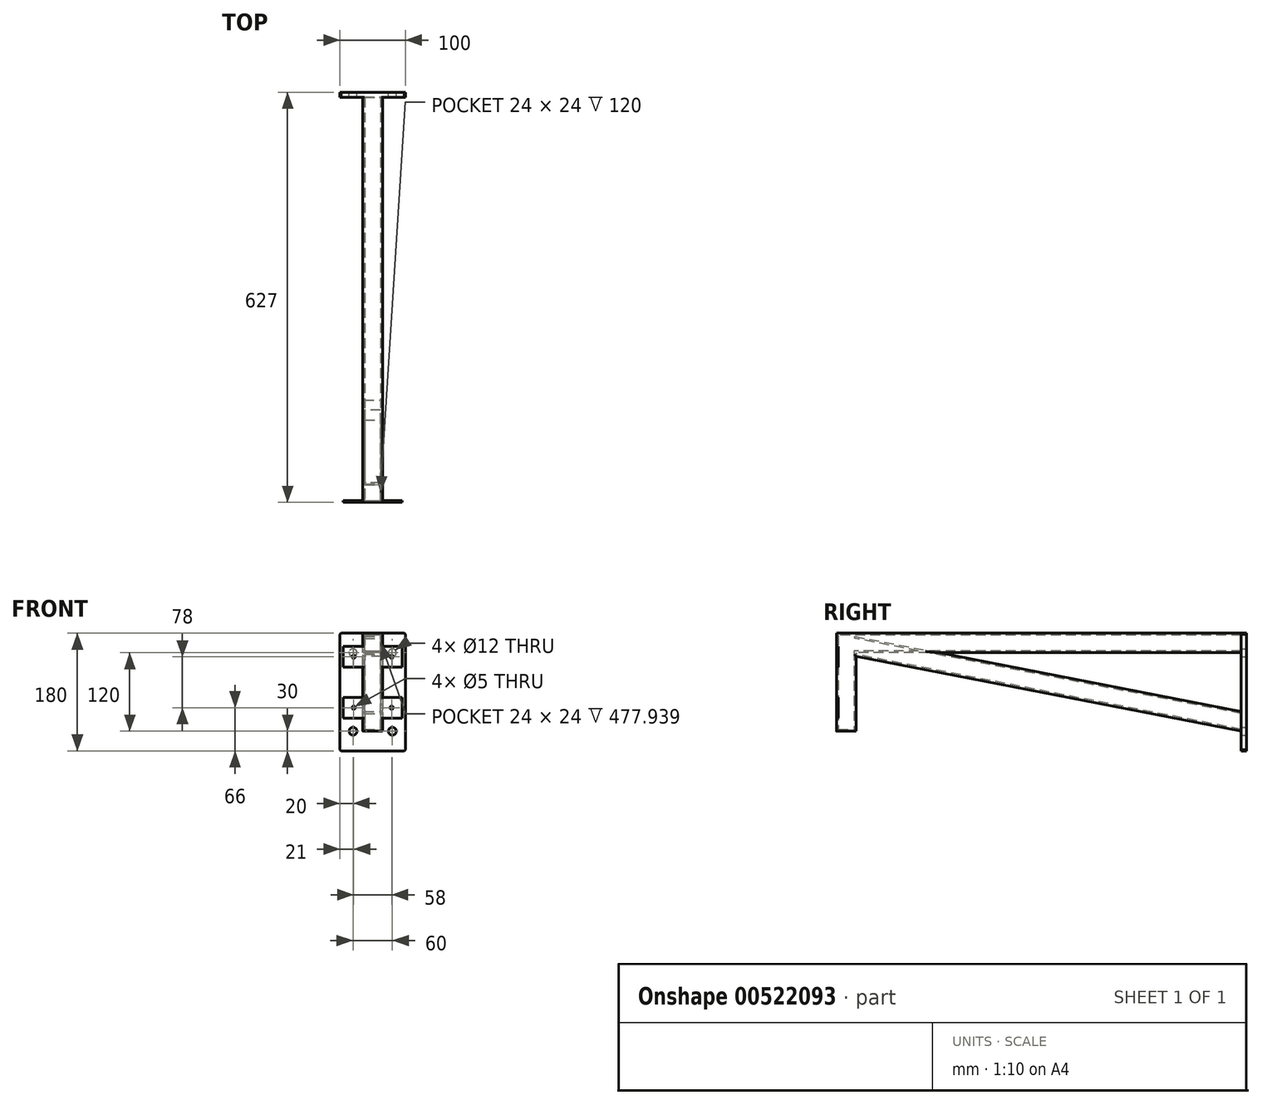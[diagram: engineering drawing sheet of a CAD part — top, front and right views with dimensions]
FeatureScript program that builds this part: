
annotation { "Feature Type Name" : "Feature", "Feature Type Description" : "" }
export const myFeature = defineFeature(function(context is Context, id is Id, definition is map)
    precondition{}
    {
        {
            var Q0;
            Q0=qCreatedBy(makeId("Front.planeOp"),FACE);
            var sketch = newSketch(context, id + "F0", { "sketchPlane" : qUnion([Q0])});
            skLineSegment(sketch, "E0.bottom", {"start": v(50, 90) * mm, "end": v(-50, 90) * mm});
            skLineSegment(sketch, "E0.top", {"start": v(50, -90) * mm, "end": v(-50, -90) * mm});
            skLineSegment(sketch, "E0.left", {"start": v(50, 90) * mm, "end": v(50, -90) * mm});
            skLineSegment(sketch, "E0.right", {"start": v(-50, 90) * mm, "end": v(-50, -90) * mm});
            skPoint(sketch, "E0.middle", {"position": v(0, 0) * mm});
            skCircle(sketch, "E1", {"center": v(-30, 60) * mm, "radius": 6 * mm});
            skCircle(sketch, "E2", {"center": v(30, 60) * mm, "radius": 6 * mm});
            skCircle(sketch, "E3", {"center": v(30, -60) * mm, "radius": 6 * mm});
            skCircle(sketch, "E4", {"center": v(-30, -60) * mm, "radius": 6 * mm});
            skSolve(sketch);
        }
        {
            var Q0;
            Q0 = qSketchRegion(id + "F0", true);
            extrude(context, id + "F1", {"entities" : qUnion([Q0]), "depth" : 8 * mm, "offsetDistance" : 25 * mm});
        }
        {
            var Q0;
            Q0=makeQuery(id+"F1.opExtrude","SWEPT_EDGE",EDGE,{"disambiguationData":[OSD([sQuery(id+"F0.wireOp",EDGE,"E0.bottom"),sQuery(id+"F0.wireOp",EDGE,"E0.left")])]});
            var Q1;
            Q1=makeQuery(id+"F1.opExtrude","SWEPT_EDGE",EDGE,{"disambiguationData":[OSD([sQuery(id+"F0.wireOp",EDGE,"E0.top"),sQuery(id+"F0.wireOp",EDGE,"E0.left")])]});
            var Q2;
            Q2=makeQuery(id+"F1.opExtrude","SWEPT_EDGE",EDGE,{"disambiguationData":[OSD([sQuery(id+"F0.wireOp",EDGE,"E0.top"),sQuery(id+"F0.wireOp",EDGE,"E0.right")])]});
            var Q3;
            Q3=makeQuery(id+"F1.opExtrude","SWEPT_EDGE",EDGE,{"disambiguationData":[OSD([sQuery(id+"F0.wireOp",EDGE,"E0.bottom"),sQuery(id+"F0.wireOp",EDGE,"E0.right")])]});
            chamfer(context, id + "F2", {"entities" : qUnion([Q0, Q1, Q2, Q3]), "width" : 2 * mm, "tangentPropagation" : true});
        }
        {
            var Q0;
            Q0=qCreatedBy(makeId("Right.planeOp"),FACE);
            var sketch = newSketch(context, id + "F3", { "sketchPlane" : qUnion([Q0])});
            skLineSegment(sketch, "E5", {"start": v(-8, 90) * mm, "end": v(-627, 90) * mm});
            skLineSegment(sketch, "E6", {"start": v(-627, 90) * mm, "end": v(-627, -57) * mm});
            skLineSegment(sketch, "E7", {"start": v(-599, 55) * mm, "end": v(-8, -60) * mm});
            skSolve(sketch);
        }
        {
            var Q0;
            Q0=makeQuery(id+"F1.opExtrude","CAP_FACE",FACE,{"disambiguationData":[OSD([sQuery(id+"F0.wireOp",EDGE,"E0.bottom"),sQuery(id+"F0.wireOp",EDGE,"E0.top"),sQuery(id+"F0.wireOp",EDGE,"E0.left"),sQuery(id+"F0.wireOp",EDGE,"E0.right"),sQuery(id+"F0.wireOp",EDGE,"E1"),sQuery(id+"F0.wireOp",EDGE,"E2"),sQuery(id+"F0.wireOp",EDGE,"E3"),sQuery(id+"F0.wireOp",EDGE,"E4")])],"isStart":false});
            var sketch = newSketch(context, id + "F4", { "sketchPlane" : qUnion([Q0])});
            skLineSegment(sketch, "E8.bottom", {"start": v(-13, 90) * mm, "end": v(13, 90) * mm});
            skLineSegment(sketch, "E8.top", {"start": v(-13, 60) * mm, "end": v(13, 60) * mm});
            skLineSegment(sketch, "E8.left", {"start": v(-15, 88) * mm, "end": v(-15, 62) * mm});
            skLineSegment(sketch, "E8.right", {"start": v(15, 88) * mm, "end": v(15, 62) * mm});
            skLineSegment(sketch, "E9.0", {"start": v(-12, 87) * mm, "end": v(12, 87) * mm});
            skLineSegment(sketch, "E9.1", {"start": v(-12, 87) * mm, "end": v(-12, 63) * mm});
            skLineSegment(sketch, "E9.2", {"start": v(-12, 63) * mm, "end": v(12, 63) * mm});
            skLineSegment(sketch, "E9.3", {"start": v(12, 87) * mm, "end": v(12, 63) * mm});
            skPoint(sketch, "E10.visualSharp", {"position": v(-15, 90) * mm});
            skArc(sketch, "E10.filletArc", {"start": v(-13, 90) * mm, "mid": v(-14.41, 89.41) * mm, "end": v(-15, 88) * mm});
            skPoint(sketch, "E11.visualSharp", {"position": v(15, 90) * mm});
            skArc(sketch, "E11.filletArc", {"start": v(15, 88) * mm, "mid": v(14.41, 89.41) * mm, "end": v(13, 90) * mm});
            skPoint(sketch, "E12.visualSharp", {"position": v(15, 60) * mm});
            skArc(sketch, "E12.filletArc", {"start": v(13, 60) * mm, "mid": v(14.41, 60.59) * mm, "end": v(15, 62) * mm});
            skPoint(sketch, "E13.visualSharp", {"position": v(-15, 60) * mm});
            skArc(sketch, "E13.filletArc", {"start": v(-15, 62) * mm, "mid": v(-14.41, 60.59) * mm, "end": v(-13, 60) * mm});
            skLineSegment(sketch, "E14.0.1.0", {"start": v(-13, -30) * mm, "end": v(13, -30) * mm});
            skLineSegment(sketch, "E14.0.1.1", {"start": v(-15, -32) * mm, "end": v(-15, -58) * mm});
            skPoint(sketch, "E14.0.1.2", {"position": v(15, -30) * mm});
            skLineSegment(sketch, "E14.0.1.3", {"start": v(-12, -33) * mm, "end": v(12, -33) * mm});
            skLineSegment(sketch, "E14.0.1.4", {"start": v(-12, -33) * mm, "end": v(-12, -57) * mm});
            skLineSegment(sketch, "E14.0.1.5", {"start": v(-13, -60) * mm, "end": v(13, -60) * mm});
            skLineSegment(sketch, "E14.0.1.6", {"start": v(-12, -57) * mm, "end": v(12, -57) * mm});
            skPoint(sketch, "E14.0.1.7", {"position": v(-15, -30) * mm});
            skPoint(sketch, "E14.0.1.8", {"position": v(15, -60) * mm});
            skLineSegment(sketch, "E14.0.1.9", {"start": v(15, -32) * mm, "end": v(15, -58) * mm});
            skPoint(sketch, "E14.0.1.10", {"position": v(-15, -60) * mm});
            skLineSegment(sketch, "E14.0.1.11", {"start": v(12, -33) * mm, "end": v(12, -57) * mm});
            skArc(sketch, "E14.0.1.12", {"start": v(-15, -58) * mm, "mid": v(-14.41, -59.41) * mm, "end": v(-13, -60) * mm});
            skArc(sketch, "E14.0.1.13", {"start": v(13, -60) * mm, "mid": v(14.41, -59.41) * mm, "end": v(15, -58) * mm});
            skArc(sketch, "E14.0.1.14", {"start": v(15, -32) * mm, "mid": v(14.41, -30.59) * mm, "end": v(13, -30) * mm});
            skArc(sketch, "E14.0.1.15", {"start": v(-13, -30) * mm, "mid": v(-14.41, -30.59) * mm, "end": v(-15, -32) * mm});
            skLineSegment(sketch, "E14.direction1", {"start": v(-15, 60) * mm, "end": v(10, 60) * mm, "construction": true});
            skLineSegment(sketch, "E14.direction2", {"start": v(-15, 60) * mm, "end": v(-15, -60) * mm, "construction": true});
            skSolve(sketch);
        }
        {
            var Q0;
            Q0=makeQuery(id+"F4.imprint","IMPRINT",FACE,{"disambiguationData":[TD([[makeQuery(id+"F4.imprint","IMPRINT",EDGE,{"derivedFrom":sQuery(id+"F4.wireOp",EDGE,"E8.bottom")}),1.0]])]});
            var Q1;
            Q1=sQuery(id+"F3.wireOp",EDGE,"E5");
            var Q2;
            Q2=sQuery(id+"F3.wireOp",EDGE,"E6");
            sweep(context, id + "F5", {"profiles" : qUnion([Q0]), "path" : qUnion([Q1, Q2])});
        }
        {
            var Q0;
            Q0=makeQuery(id+"F4.imprint","IMPRINT",FACE,{"disambiguationData":[TD([[makeQuery(id+"F4.imprint","IMPRINT",EDGE,{"derivedFrom":sQuery(id+"F4.wireOp",EDGE,"E14.0.1.0")}),-1.0]])]});
            var Q1;
            Q1=sQuery(id+"F3.wireOp",EDGE,"E7");
            sweep(context, id + "F6", {"operationType" : NewBodyOperationType.ADD, "profiles" : qUnion([Q0]), "path" : qUnion([Q1]), "keepProfileOrientation" : true});
        }
        {
            var Q0;
            Q0=makeQuery(id+"F5.opSweep","CAP_FACE",FACE,{"disambiguationData":[OSD([sQuery(id+"F3.wireOp",VERTEX,"E6.end"),sQuery(id+"F4.wireOp",EDGE,"E8.bottom"),sQuery(id+"F4.wireOp",EDGE,"E8.top"),sQuery(id+"F4.wireOp",EDGE,"E8.left"),sQuery(id+"F4.wireOp",EDGE,"E8.right"),sQuery(id+"F4.wireOp",EDGE,"E9.0"),sQuery(id+"F4.wireOp",EDGE,"E9.1"),sQuery(id+"F4.wireOp",EDGE,"E9.2"),sQuery(id+"F4.wireOp",EDGE,"E9.3"),sQuery(id+"F4.wireOp",EDGE,"E10.filletArc"),sQuery(id+"F4.wireOp",EDGE,"E11.filletArc"),sQuery(id+"F4.wireOp",EDGE,"E12.filletArc"),sQuery(id+"F4.wireOp",EDGE,"E13.filletArc")])],"isStart":false});
            var sketch = newSketch(context, id + "F7", { "sketchPlane" : qUnion([Q0])});
            skLineSegment(sketch, "E15.0", {"start": v(-15, 625) * mm, "end": v(-15, 599) * mm});
            skPoint(sketch, "E16.0", {"position": v(-14.41, 597.59) * mm});
            skArc(sketch, "E17.0", {"start": v(-15, 599) * mm, "mid": v(-14.41, 597.59) * mm, "end": v(-13, 597) * mm});
            skLineSegment(sketch, "E18.0", {"start": v(-13, 597) * mm, "end": v(13, 597) * mm});
            skArc(sketch, "E19.0", {"start": v(13, 597) * mm, "mid": v(14.41, 597.59) * mm, "end": v(15, 599) * mm});
            skLineSegment(sketch, "E20.0", {"start": v(15, 625) * mm, "end": v(15, 599) * mm});
            skArc(sketch, "E21.0", {"start": v(15, 625) * mm, "mid": v(14.41, 626.41) * mm, "end": v(13, 627) * mm});
            skLineSegment(sketch, "E22.0", {"start": v(13, 627) * mm, "end": v(-13, 627) * mm});
            skArc(sketch, "E23.0", {"start": v(-13, 627) * mm, "mid": v(-14.41, 626.41) * mm, "end": v(-15, 625) * mm});
            skSolve(sketch);
        }
        {
            var Q0;
            Q0 = qSketchRegion(id + "F7", true);
            extrude(context, id + "F8", {"entities" : qUnion([Q0]), "operationType" : NewBodyOperationType.ADD, "depth" : 3 * mm, "offsetDistance" : 25 * mm});
        }
        {
            var Q0;
            Q0=makeQuery(id+"F8.boolean.opBoolean","MERGE",FACE,{"derivedFrom":[makeQuery(id+"F5.opSweep","SWEPT_FACE",FACE,{"disambiguationData":[OSD([sQuery(id+"F3.wireOp",EDGE,"E6"),sQuery(id+"F4.wireOp",EDGE,"E8.bottom")])]}),makeQuery(id+"F8.opExtrude","SWEPT_FACE",FACE,{"disambiguationData":[OSD([sQuery(id+"F7.wireOp",EDGE,"E22.0")])]})]});
            var sketch = newSketch(context, id + "F9", { "sketchPlane" : qUnion([Q0])});
            skLineSegment(sketch, "E24.bottom", {"start": v(13, 70) * mm, "end": v(45, 70) * mm});
            skLineSegment(sketch, "E24.top", {"start": v(13, 38) * mm, "end": v(45, 38) * mm});
            skLineSegment(sketch, "E24.left", {"start": v(13, 70) * mm, "end": v(13, 38) * mm});
            skLineSegment(sketch, "E24.right", {"start": v(45, 70) * mm, "end": v(45, 38) * mm});
            skLineSegment(sketch, "E25.bottom", {"start": v(13, -8) * mm, "end": v(45, -8) * mm});
            skLineSegment(sketch, "E25.top", {"start": v(13, -40) * mm, "end": v(45, -40) * mm});
            skLineSegment(sketch, "E25.left", {"start": v(13, -8) * mm, "end": v(13, -40) * mm});
            skLineSegment(sketch, "E25.right", {"start": v(45, -8) * mm, "end": v(45, -40) * mm});
            skCircle(sketch, "E26", {"center": v(29, 54) * mm, "radius": 2.5 * mm});
            skPoint(sketch, "E26.centerSnap0", {"position": v(45, 54) * mm});
            skPoint(sketch, "E27", {"position": v(13, 54) * mm});
            skCircle(sketch, "E28", {"center": v(29, -24) * mm, "radius": 2.5 * mm});
            skPoint(sketch, "E28.centerSnap0", {"position": v(29, -40) * mm});
            skPoint(sketch, "E29", {"position": v(45, -24) * mm});
            skLineSegment(sketch, "E30.MirrorCS", {"start": v(-13, -8) * mm, "end": v(-45, -8) * mm});
            skPoint(sketch, "E31.MirrorP", {"position": v(-45, -24) * mm});
            skLineSegment(sketch, "E32.MirrorCS", {"start": v(-45, -8) * mm, "end": v(-45, -40) * mm});
            skLineSegment(sketch, "E33.MirrorCS", {"start": v(-13, -8) * mm, "end": v(-13, -40) * mm});
            skPoint(sketch, "E34.MirrorP", {"position": v(-29, -40) * mm});
            skCircle(sketch, "E35.MirrorC", {"center": v(-29, -24) * mm, "radius": 2.5 * mm});
            skLineSegment(sketch, "E36.MirrorCS", {"start": v(-13, -40) * mm, "end": v(-45, -40) * mm});
            skPoint(sketch, "E37.MirrorP", {"position": v(-45, 54) * mm});
            skLineSegment(sketch, "E38.MirrorCS", {"start": v(-45, 70) * mm, "end": v(-45, 38) * mm});
            skLineSegment(sketch, "E39.MirrorCS", {"start": v(-13, 38) * mm, "end": v(-45, 38) * mm});
            skLineSegment(sketch, "E40.MirrorCS", {"start": v(-13, 70) * mm, "end": v(-45, 70) * mm});
            skLineSegment(sketch, "E41.MirrorCS", {"start": v(-13, 70) * mm, "end": v(-13, 38) * mm});
            skPoint(sketch, "E42.MirrorP", {"position": v(-13, 54) * mm});
            skCircle(sketch, "E43.MirrorC", {"center": v(-29, 54) * mm, "radius": 2.5 * mm});
            skSolve(sketch);
        }
        {
            var Q0;
            Q0 = qSketchRegion(id + "F9", true);
            extrude(context, id + "F10", {"entities" : qUnion([Q0]), "operationType" : NewBodyOperationType.ADD, "oppositeDirection" : true, "depth" : 3 * mm, "offsetDistance" : 25 * mm});
        }
    });
